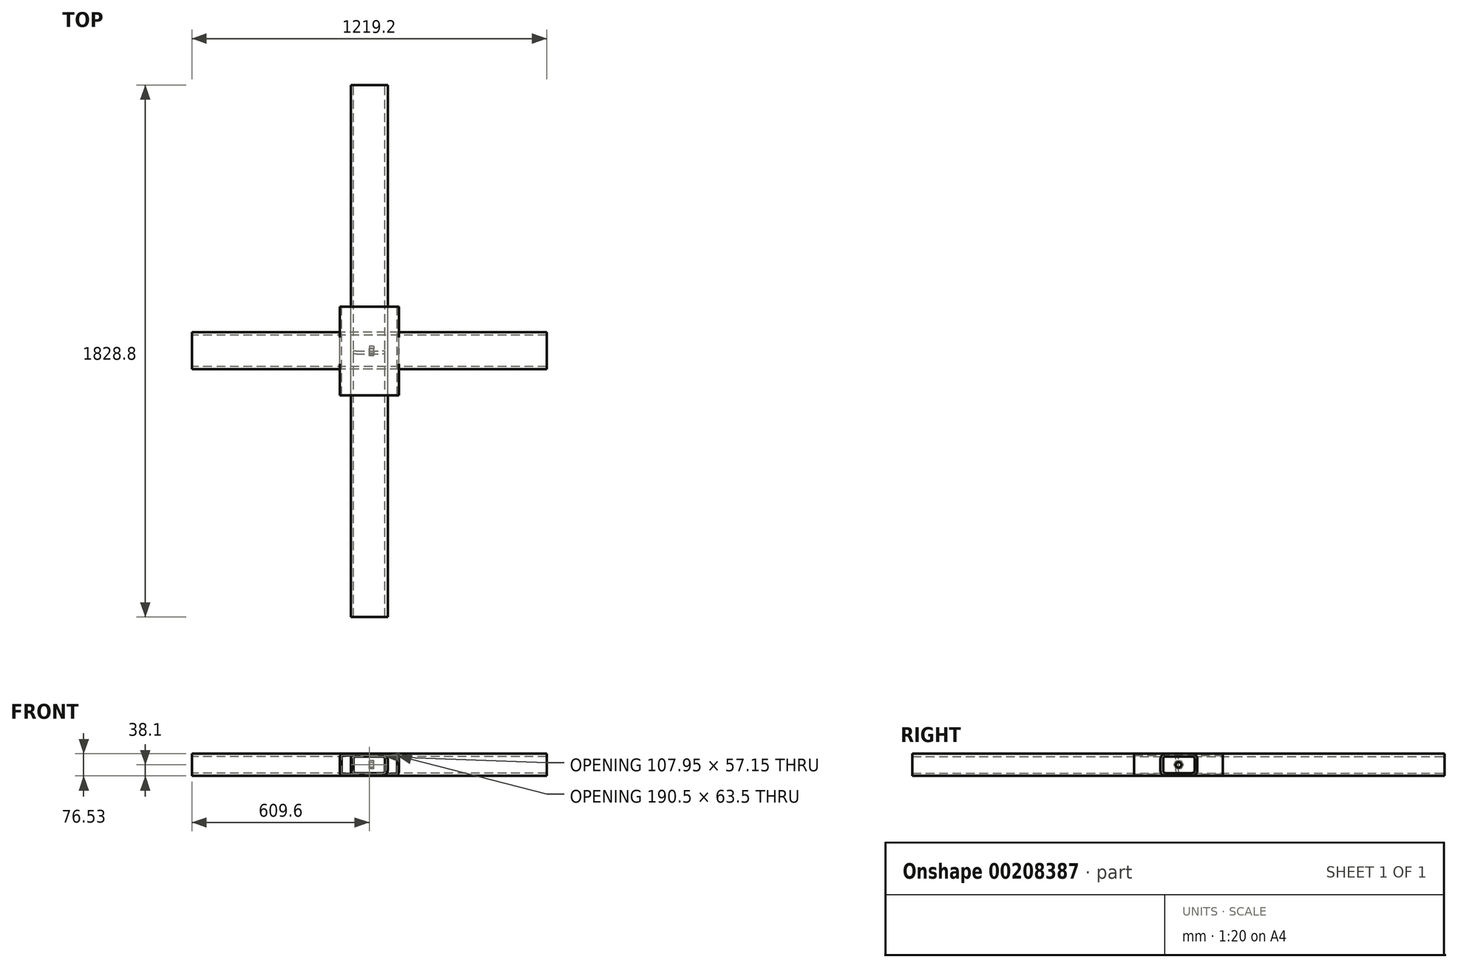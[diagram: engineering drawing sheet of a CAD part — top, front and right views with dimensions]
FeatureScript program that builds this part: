
annotation { "Feature Type Name" : "Feature", "Feature Type Description" : "" }
export const myFeature = defineFeature(function(context is Context, id is Id, definition is map)
    precondition{}
    {
        {
            var Q0;
            Q0=qCreatedBy(makeId("Front.planeOp"),FACE);
            var sketch = newSketch(context, id + "F0", { "sketchPlane" : qUnion([Q0])});
            skLineSegment(sketch, "E0.bottom", {"start": v(88.11, 38.1) * mm, "end": v(-88.11, 38.1) * mm});
            skLineSegment(sketch, "E0.top", {"start": v(88.11, -38.1) * mm, "end": v(-88.11, -38.1) * mm});
            skLineSegment(sketch, "E0.left", {"start": v(101.6, 24.61) * mm, "end": v(101.6, -24.61) * mm});
            skLineSegment(sketch, "E0.right", {"start": v(-101.6, 24.61) * mm, "end": v(-101.6, -24.61) * mm});
            skPoint(sketch, "E0.middle", {"position": v(0, 0) * mm});
            skPoint(sketch, "E1.visualSharp", {"position": v(-101.6, 38.1) * mm});
            skPoint(sketch, "E2.visualSharp", {"position": v(101.6, 38.1) * mm});
            skPoint(sketch, "E3.visualSharp", {"position": v(101.6, -38.1) * mm});
            skPoint(sketch, "E4.visualSharp", {"position": v(-101.6, -38.1) * mm});
            skPoint(sketch, "E5.endSnap0", {"position": v(0, 38.1) * mm});
            skLineSegment(sketch, "E6.bottom", {"start": v(-88.11, 31.75) * mm, "end": v(88.11, 31.75) * mm});
            skLineSegment(sketch, "E6.top", {"start": v(-88.11, -31.75) * mm, "end": v(88.11, -31.75) * mm});
            skLineSegment(sketch, "E6.left", {"start": v(-95.25, 24.61) * mm, "end": v(-95.25, -24.61) * mm});
            skLineSegment(sketch, "E6.right", {"start": v(95.25, 24.61) * mm, "end": v(95.25, -24.61) * mm});
            skPoint(sketch, "E7.visualSharp", {"position": v(-95.25, 31.75) * mm});
            skArc(sketch, "E7.filletArc", {"start": v(-88.11, 31.75) * mm, "mid": v(-93.16, 29.66) * mm, "end": v(-95.25, 24.61) * mm});
            skArc(sketch, "E8.0", {"start": v(-88.11, 38.1) * mm, "mid": v(-97.65, 34.15) * mm, "end": v(-101.6, 24.61) * mm});
            skPoint(sketch, "E9.visualSharp", {"position": v(95.25, 31.75) * mm});
            skArc(sketch, "E9.filletArc", {"start": v(95.25, 24.61) * mm, "mid": v(93.16, 29.66) * mm, "end": v(88.11, 31.75) * mm});
            skPoint(sketch, "E10.visualSharp", {"position": v(95.25, -31.75) * mm});
            skArc(sketch, "E10.filletArc", {"start": v(88.11, -31.75) * mm, "mid": v(93.16, -29.66) * mm, "end": v(95.25, -24.61) * mm});
            skPoint(sketch, "E11.visualSharp", {"position": v(-95.25, -31.75) * mm});
            skArc(sketch, "E11.filletArc", {"start": v(-95.25, -24.61) * mm, "mid": v(-93.16, -29.66) * mm, "end": v(-88.11, -31.75) * mm});
            skArc(sketch, "E12.0", {"start": v(-101.6, -24.61) * mm, "mid": v(-97.65, -34.15) * mm, "end": v(-88.11, -38.1) * mm});
            skArc(sketch, "E13.0", {"start": v(101.6, 24.61) * mm, "mid": v(97.65, 34.15) * mm, "end": v(88.11, 38.1) * mm});
            skArc(sketch, "E14.0", {"start": v(88.11, -38.1) * mm, "mid": v(97.65, -34.15) * mm, "end": v(101.6, -24.61) * mm});
            skSolve(sketch);
        }
        {
            var Q0;
            Q0=makeQuery(id+"F0.imprint","IMPRINT",FACE,{"disambiguationData":[TD([[makeQuery(id+"F0.imprint","IMPRINT",EDGE,{"derivedFrom":sQuery(id+"F0.wireOp",EDGE,"E0.bottom")}),1.0]])]});
            extrude(context, id + "F1", {"entities" : qUnion([Q0]), "endBound" : BoundingType.SYMMETRIC, "depth" : 304.8 * mm});
        }
        {
            var Q0;
            Q0=makeQuery(id+"F1.opExtrude","SWEPT_FACE",FACE,{"disambiguationData":[OSD([sQuery(id+"F0.wireOp",EDGE,"E0.left")])]});
            var sketch = newSketch(context, id + "F2", { "sketchPlane" : qUnion([Q0])});
            skPoint(sketch, "E15", {"position": v(0, 0) * mm});
            skSolve(sketch);
        }
        {
            var Q0;
            Q0=sQuery(id+"F2.wireOp",VERTEX,"E15");
            var Q1;
            Q1=makeQuery(id+"F1.opExtrude","SWEPT_BODY",BODY,{"disambiguationData":[OSD([sQuery(id+"F0.wireOp",EDGE,"E0.bottom"),sQuery(id+"F0.wireOp",EDGE,"E0.top"),sQuery(id+"F0.wireOp",EDGE,"E0.left"),sQuery(id+"F0.wireOp",EDGE,"E0.right"),sQuery(id+"F0.wireOp",EDGE,"E6.bottom"),sQuery(id+"F0.wireOp",EDGE,"E6.top"),sQuery(id+"F0.wireOp",EDGE,"E6.left"),sQuery(id+"F0.wireOp",EDGE,"E6.right"),sQuery(id+"F0.wireOp",EDGE,"E7.filletArc"),sQuery(id+"F0.wireOp",EDGE,"E8.0"),sQuery(id+"F0.wireOp",EDGE,"E9.filletArc"),sQuery(id+"F0.wireOp",EDGE,"E10.filletArc"),sQuery(id+"F0.wireOp",EDGE,"E11.filletArc"),sQuery(id+"F0.wireOp",EDGE,"E12.0"),sQuery(id+"F0.wireOp",EDGE,"E13.0"),sQuery(id+"F0.wireOp",EDGE,"E14.0")])]});
            hole(context, id + "F3", {"style" : HoleStyle.SIMPLE, "endStyle" : HoleEndStyle.BLIND, "holeDiameter" : 19.05 * mm, "holeDepth" : 12.7 * mm, "locations" : qUnion([Q0]), "scope" : qUnion([Q1])});
        }
        {
            var Q0;
            Q0=qCreatedBy(makeId("Right.planeOp"),FACE);
            var sketch = newSketch(context, id + "F4", { "sketchPlane" : qUnion([Q0])});
            skCircle(sketch, "E16.cCircle", {"center": v(0, 0) * mm, "radius": 13.9 * mm, "construction": true});
            skLineSegment(sketch, "E16.0", {"start": v(-8.02, 13.9) * mm, "end": v(8.02, 13.9) * mm});
            skLineSegment(sketch, "E16.1", {"start": v(8.02, 13.9) * mm, "end": v(16.04, 0) * mm});
            skLineSegment(sketch, "E16.2", {"start": v(16.04, 0) * mm, "end": v(8.02, -13.9) * mm});
            skLineSegment(sketch, "E16.3", {"start": v(8.02, -13.9) * mm, "end": v(-8.02, -13.9) * mm});
            skLineSegment(sketch, "E16.4", {"start": v(-8.02, -13.9) * mm, "end": v(-16.04, 0) * mm});
            skLineSegment(sketch, "E16.5", {"start": v(-16.04, 0) * mm, "end": v(-8.02, 13.9) * mm});
            skPoint(sketch, "E16.0.midPoint", {"position": v(0, 13.9) * mm});
            skSolve(sketch);
        }
        {
            var Q0;
            Q0=makeQuery(id+"F4.imprint","IMPRINT",FACE,{"disambiguationData":[TD([[makeQuery(id+"F4.imprint","IMPRINT",EDGE,{"derivedFrom":sQuery(id+"F4.wireOp",EDGE,"E16.0")}),-1.0]])]});
            extrude(context, id + "F5", {"entities" : qUnion([Q0]), "depth" : 16.26 * mm});
        }
        {
            var Q0;
            Q0=sQuery(id+"F4.wireOp",VERTEX,"E16.cCircle.center");
            var Q1;
            Q1=makeQuery(id+"F5.opExtrude","SWEPT_BODY",BODY,{"disambiguationData":[OSD([sQuery(id+"F4.wireOp",EDGE,"E16.0"),sQuery(id+"F4.wireOp",EDGE,"E16.1"),sQuery(id+"F4.wireOp",EDGE,"E16.2"),sQuery(id+"F4.wireOp",EDGE,"E16.3"),sQuery(id+"F4.wireOp",EDGE,"E16.4"),sQuery(id+"F4.wireOp",EDGE,"E16.5")])]});
            hole(context, id + "F6", {"style" : HoleStyle.SIMPLE, "endStyle" : HoleEndStyle.THROUGH, "oppositeDirection" : true, "standardTappedOrClearance" : lookupTablePath({ "standard" : "ANSI", "engagement" : "75%", "pitch" : "10 tpi", "size" : "3/4", "type" : "Tapped" }), "standardBlindInLast" : lookupTablePath({ "standard" : "ANSI", "engagement" : "75%", "pitch" : "10 tpi", "size" : "3/4", "type" : "Tapped" }), "holeDiameter" : 16.67 * mm, "startFromSketch" : true, "locations" : qUnion([Q0]), "scope" : qUnion([Q1]), "isTappedThrough" : true, "majorDiameter" : 19.05 * mm, "showTappedDepth" : true});
        }
        {
            var Q0;
            Q0=qCreatedBy(makeId("Front.planeOp"),FACE);
            var sketch = newSketch(context, id + "F7", { "sketchPlane" : qUnion([Q0])});
            skPoint(sketch, "E17.middle", {"position": v(0, 0) * mm});
            skLineSegment(sketch, "E18.bottom", {"start": v(-45.26, -28.58) * mm, "end": v(45.26, -28.58) * mm});
            skLineSegment(sketch, "E18.top", {"start": v(-45.26, 28.58) * mm, "end": v(45.26, 28.58) * mm});
            skLineSegment(sketch, "E18.left", {"start": v(-53.97, -19.86) * mm, "end": v(-53.98, 19.86) * mm});
            skLineSegment(sketch, "E18.right", {"start": v(53.98, -19.86) * mm, "end": v(53.97, 19.86) * mm});
            skPoint(sketch, "E19.visualSharp", {"position": v(-53.98, 28.58) * mm});
            skArc(sketch, "E19.filletArc", {"start": v(-45.26, 28.58) * mm, "mid": v(-51.42, 26.02) * mm, "end": v(-53.98, 19.86) * mm});
            skPoint(sketch, "E20.visualSharp", {"position": v(53.97, 28.58) * mm});
            skArc(sketch, "E20.filletArc", {"start": v(53.97, 19.86) * mm, "mid": v(51.42, 26.02) * mm, "end": v(45.26, 28.58) * mm});
            skPoint(sketch, "E21.visualSharp", {"position": v(53.98, -28.58) * mm});
            skArc(sketch, "E21.filletArc", {"start": v(45.26, -28.58) * mm, "mid": v(51.42, -26.02) * mm, "end": v(53.98, -19.86) * mm});
            skPoint(sketch, "E22.visualSharp", {"position": v(-53.97, -28.58) * mm});
            skArc(sketch, "E22.filletArc", {"start": v(-53.97, -19.86) * mm, "mid": v(-51.42, -26.02) * mm, "end": v(-45.26, -28.58) * mm});
            skArc(sketch, "E23.0", {"start": v(-45.26, 38.1) * mm, "mid": v(-58.16, 32.76) * mm, "end": v(-63.5, 19.86) * mm});
            skArc(sketch, "E24.0", {"start": v(63.5, 19.86) * mm, "mid": v(58.16, 32.76) * mm, "end": v(45.26, 38.1) * mm});
            skArc(sketch, "E25.0", {"start": v(45.26, -38.1) * mm, "mid": v(58.16, -32.76) * mm, "end": v(63.5, -19.86) * mm});
            skArc(sketch, "E26.0", {"start": v(-63.5, -19.86) * mm, "mid": v(-58.16, -32.76) * mm, "end": v(-45.26, -38.1) * mm});
            skLineSegment(sketch, "E27", {"start": v(63.5, 19.86) * mm, "end": v(63.5, -19.86) * mm});
            skLineSegment(sketch, "E28", {"start": v(45.26, 38.1) * mm, "end": v(-45.26, 38.1) * mm});
            skLineSegment(sketch, "E29", {"start": v(-63.5, 19.86) * mm, "end": v(-63.5, -19.86) * mm});
            skLineSegment(sketch, "E30", {"start": v(-45.26, -38.1) * mm, "end": v(45.26, -38.1) * mm});
            skSolve(sketch);
        }
        {
            var Q0;
            Q0=makeQuery(id+"F7.imprint","IMPRINT",FACE,{"disambiguationData":[TD([[makeQuery(id+"F7.imprint","IMPRINT",EDGE,{"derivedFrom":sQuery(id+"F7.wireOp",EDGE,"E18.bottom")}),-1.0]])]});
            extrude(context, id + "F8", {"entities" : qUnion([Q0]), "endBound" : BoundingType.SYMMETRIC, "depth" : 1828.8 * mm});
        }
        {
            var Q0;
            Q0=qCreatedBy(makeId("Right.planeOp"),FACE);
            var sketch = newSketch(context, id + "F9", { "sketchPlane" : qUnion([Q0])});
            skPoint(sketch, "E31.middle", {"position": v(1.3, 0.33) * mm});
            skLineSegment(sketch, "E32.bottom", {"start": v(-43.95, -28.25) * mm, "end": v(46.57, -28.25) * mm});
            skLineSegment(sketch, "E32.top", {"start": v(-43.95, 28.9) * mm, "end": v(46.57, 28.9) * mm});
            skLineSegment(sketch, "E32.left", {"start": v(-52.67, -19.54) * mm, "end": v(-52.67, 20.2) * mm});
            skLineSegment(sketch, "E32.right", {"start": v(55.28, -19.54) * mm, "end": v(55.28, 20.2) * mm});
            skPoint(sketch, "E33.visualSharp", {"position": v(-52.67, 28.9) * mm});
            skArc(sketch, "E33.filletArc", {"start": v(-43.95, 28.9) * mm, "mid": v(-50.11, 26.35) * mm, "end": v(-52.67, 20.2) * mm});
            skPoint(sketch, "E34.visualSharp", {"position": v(55.28, 28.9) * mm});
            skArc(sketch, "E34.filletArc", {"start": v(55.28, 20.2) * mm, "mid": v(52.73, 26.35) * mm, "end": v(46.57, 28.9) * mm});
            skPoint(sketch, "E35.visualSharp", {"position": v(55.28, -28.25) * mm});
            skArc(sketch, "E35.filletArc", {"start": v(46.57, -28.25) * mm, "mid": v(52.73, -25.7) * mm, "end": v(55.28, -19.54) * mm});
            skPoint(sketch, "E36.visualSharp", {"position": v(-52.67, -28.25) * mm});
            skArc(sketch, "E36.filletArc", {"start": v(-52.67, -19.54) * mm, "mid": v(-50.11, -25.7) * mm, "end": v(-43.95, -28.25) * mm});
            skArc(sketch, "E37.0", {"start": v(-43.95, 38.43) * mm, "mid": v(-56.85, 33.09) * mm, "end": v(-62.2, 20.2) * mm});
            skArc(sketch, "E38.0", {"start": v(64.8, 20.2) * mm, "mid": v(59.47, 33.09) * mm, "end": v(46.57, 38.43) * mm});
            skArc(sketch, "E39.0", {"start": v(46.57, -37.77) * mm, "mid": v(59.47, -32.43) * mm, "end": v(64.8, -19.54) * mm});
            skArc(sketch, "E40.0", {"start": v(-62.2, -19.54) * mm, "mid": v(-56.85, -32.43) * mm, "end": v(-43.95, -37.77) * mm});
            skLineSegment(sketch, "E41", {"start": v(64.8, 20.2) * mm, "end": v(64.8, -19.54) * mm});
            skLineSegment(sketch, "E42", {"start": v(46.57, 38.43) * mm, "end": v(-43.95, 38.43) * mm});
            skLineSegment(sketch, "E43", {"start": v(-62.2, 20.2) * mm, "end": v(-62.2, -19.54) * mm});
            skLineSegment(sketch, "E44", {"start": v(-43.95, -37.77) * mm, "end": v(46.57, -37.77) * mm});
            skSolve(sketch);
        }
        {
            var Q0;
            Q0=makeQuery(id+"F9.imprint","IMPRINT",FACE,{"disambiguationData":[TD([[makeQuery(id+"F9.imprint","IMPRINT",EDGE,{"derivedFrom":sQuery(id+"F9.wireOp",EDGE,"E32.bottom")}),-1.0]])]});
            extrude(context, id + "F10", {"entities" : qUnion([Q0]), "endBound" : BoundingType.SYMMETRIC, "depth" : 1219.2 * mm});
        }
        {
            var Q0;
            Q0=qCreatedBy(makeId("Front.planeOp"),FACE);
            var sketch = newSketch(context, id + "F11", { "sketchPlane" : qUnion([Q0])});
            skLineSegment(sketch, "E45.bottom", {"start": v(-45.48, -28.47) * mm, "end": v(45.04, -28.47) * mm});
            skLineSegment(sketch, "E45.top", {"start": v(-45.48, 28.68) * mm, "end": v(45.04, 28.68) * mm});
            skLineSegment(sketch, "E45.left", {"start": v(-54.2, -19.75) * mm, "end": v(-54.2, 19.97) * mm});
            skLineSegment(sketch, "E45.right", {"start": v(53.76, -19.75) * mm, "end": v(53.76, 19.97) * mm});
            skArc(sketch, "E46.filletArc", {"start": v(-45.48, 28.68) * mm, "mid": v(-51.64, 26.13) * mm, "end": v(-54.2, 19.97) * mm});
            skArc(sketch, "E47.filletArc", {"start": v(53.76, 19.97) * mm, "mid": v(51.2, 26.13) * mm, "end": v(45.04, 28.68) * mm});
            skArc(sketch, "E48.filletArc", {"start": v(45.04, -28.47) * mm, "mid": v(51.2, -25.91) * mm, "end": v(53.76, -19.75) * mm});
            skArc(sketch, "E49.filletArc", {"start": v(-54.2, -19.75) * mm, "mid": v(-51.64, -25.91) * mm, "end": v(-45.48, -28.47) * mm});
            skSolve(sketch);
        }
        {
            var Q0;
            Q0=makeQuery(id+"F11.imprint","IMPRINT",FACE,{"disambiguationData":[TD([[makeQuery(id+"F11.imprint","IMPRINT",EDGE,{"derivedFrom":sQuery(id+"F11.wireOp",EDGE,"E45.bottom")}),1.0]])]});
            extrude(context, id + "F12", {"entities" : qUnion([Q0]), "depth" : 9.52 * mm});
        }
    });
